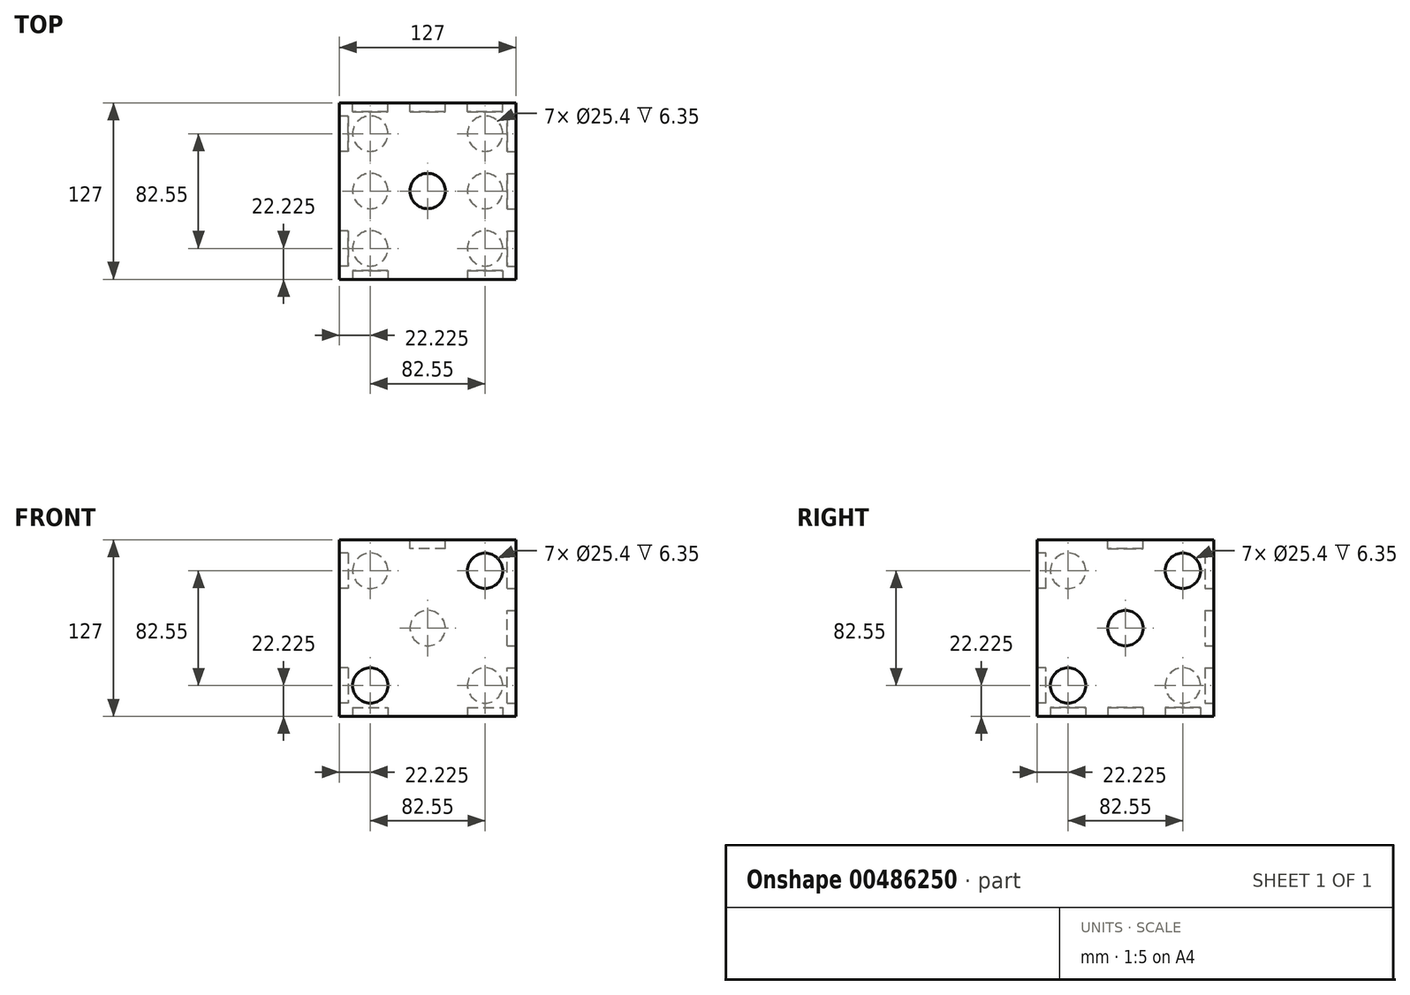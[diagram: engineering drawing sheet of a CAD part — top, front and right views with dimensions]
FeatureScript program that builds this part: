
annotation { "Feature Type Name" : "Feature", "Feature Type Description" : "" }
export const myFeature = defineFeature(function(context is Context, id is Id, definition is map)
    precondition{}
    {
        {
            var Q0;
            Q0=qCreatedBy(makeId("Top.planeOp"),FACE);
            var sketch = newSketch(context, id + "F0", { "sketchPlane" : qUnion([Q0])});
            skLineSegment(sketch, "E0.bottom", {"start": v(0, 0) * mm, "end": v(127, 0) * mm});
            skLineSegment(sketch, "E0.top", {"start": v(0, 127) * mm, "end": v(127, 127) * mm});
            skLineSegment(sketch, "E0.left", {"start": v(0, 0) * mm, "end": v(0, 127) * mm});
            skLineSegment(sketch, "E0.right", {"start": v(127, 0) * mm, "end": v(127, 127) * mm});
            skSolve(sketch);
        }
        {
            var Q0;
            Q0 = qSketchRegion(id + "F0", true);
            extrude(context, id + "F1", {"entities" : qUnion([Q0]), "depth" : 127 * mm});
        }
        {
            var Q0;
            Q0=makeQuery(id+"F1.opExtrude","CAP_FACE",FACE,{"disambiguationData":[OSD([sQuery(id+"F0.wireOp",EDGE,"E0.bottom"),sQuery(id+"F0.wireOp",EDGE,"E0.top"),sQuery(id+"F0.wireOp",EDGE,"E0.left"),sQuery(id+"F0.wireOp",EDGE,"E0.right")])],"isStart":false});
            var sketch = newSketch(context, id + "F2", { "sketchPlane" : qUnion([Q0])});
            skCircle(sketch, "E1", {"center": v(63.5, 63.5) * mm, "radius": 12.7 * mm});
            skPoint(sketch, "E1.centerSnap0", {"position": v(0, 63.5) * mm});
            skPoint(sketch, "E1.centerSnap1", {"position": v(63.5, 127) * mm});
            skSolve(sketch);
        }
        {
            var Q0;
            Q0 = qSketchRegion(id + "F2", true);
            extrude(context, id + "F3", {"entities" : qUnion([Q0]), "operationType" : NewBodyOperationType.REMOVE, "oppositeDirection" : true, "depth" : 6.35 * mm});
        }
        {
            var Q0;
            Q0=makeQuery(id+"F1.opExtrude","SWEPT_FACE",FACE,{"disambiguationData":[OSD([sQuery(id+"F0.wireOp",EDGE,"E0.bottom")])]});
            var sketch = newSketch(context, id + "F4", { "sketchPlane" : qUnion([Q0])});
            skCircle(sketch, "E2", {"center": v(22.23, 22.22) * mm, "radius": 12.7 * mm});
            skCircle(sketch, "E3", {"center": v(104.77, 104.78) * mm, "radius": 12.7 * mm});
            skSolve(sketch);
        }
        {
            var Q0;
            Q0 = qSketchRegion(id + "F4", true);
            extrude(context, id + "F5", {"entities" : qUnion([Q0]), "operationType" : NewBodyOperationType.REMOVE, "oppositeDirection" : true, "depth" : 6.35 * mm});
        }
        {
            var Q0;
            Q0=makeQuery(id+"F1.opExtrude","SWEPT_FACE",FACE,{"disambiguationData":[OSD([sQuery(id+"F0.wireOp",EDGE,"E0.right")])]});
            var sketch = newSketch(context, id + "F6", { "sketchPlane" : qUnion([Q0])});
            skCircle(sketch, "E4", {"center": v(22.23, 22.22) * mm, "radius": 12.7 * mm});
            skCircle(sketch, "E5", {"center": v(63.5, 63.5) * mm, "radius": 12.7 * mm});
            skPoint(sketch, "E5.centerSnap0", {"position": v(63.5, 127) * mm});
            skPoint(sketch, "E5.centerSnap1", {"position": v(0, 63.5) * mm});
            skCircle(sketch, "E6", {"center": v(104.77, 104.78) * mm, "radius": 12.7 * mm});
            skSolve(sketch);
        }
        {
            var Q0;
            Q0 = qSketchRegion(id + "F6", true);
            extrude(context, id + "F7", {"entities" : qUnion([Q0]), "operationType" : NewBodyOperationType.REMOVE, "oppositeDirection" : true, "depth" : 6.35 * mm});
        }
        {
            var Q0;
            Q0=makeQuery(id+"F1.opExtrude","SWEPT_FACE",FACE,{"disambiguationData":[OSD([sQuery(id+"F0.wireOp",EDGE,"E0.top")])]});
            var sketch = newSketch(context, id + "F8", { "sketchPlane" : qUnion([Q0])});
            skLineSegment(sketch, "E7", {"start": v(-127, 127) * mm, "end": v(0, 0) * mm, "construction": true});
            skLineSegment(sketch, "E8", {"start": v(0, 127) * mm, "end": v(-127, 0) * mm, "construction": true});
            skCircle(sketch, "E9", {"center": v(-63.5, 63.5) * mm, "radius": 12.7 * mm});
            skCircle(sketch, "E10", {"center": v(-22.23, 104.78) * mm, "radius": 12.7 * mm});
            skCircle(sketch, "E11", {"center": v(-104.78, 104.78) * mm, "radius": 12.7 * mm});
            skCircle(sketch, "E12", {"center": v(-104.78, 22.23) * mm, "radius": 12.7 * mm});
            skCircle(sketch, "E13", {"center": v(-22.23, 22.23) * mm, "radius": 12.7 * mm});
            skSolve(sketch);
        }
        {
            var Q0;
            Q0 = qSketchRegion(id + "F8", true);
            extrude(context, id + "F9", {"entities" : qUnion([Q0]), "operationType" : NewBodyOperationType.REMOVE, "oppositeDirection" : true, "depth" : 6.35 * mm, "offsetDistance" : 25.4 * mm});
        }
        {
            var Q0;
            Q0=makeQuery(id+"F1.opExtrude","SWEPT_FACE",FACE,{"disambiguationData":[OSD([sQuery(id+"F0.wireOp",EDGE,"E0.left")])]});
            var sketch = newSketch(context, id + "F10", { "sketchPlane" : qUnion([Q0])});
            skLineSegment(sketch, "E14", {"start": v(-127, 127) * mm, "end": v(0, 0) * mm, "construction": true});
            skLineSegment(sketch, "E15", {"start": v(0, 127) * mm, "end": v(-127, 0) * mm, "construction": true});
            skCircle(sketch, "E16", {"center": v(-104.77, 104.77) * mm, "radius": 12.7 * mm});
            skCircle(sketch, "E17", {"center": v(-22.22, 104.77) * mm, "radius": 12.7 * mm});
            skCircle(sketch, "E18", {"center": v(-22.22, 22.23) * mm, "radius": 12.7 * mm});
            skCircle(sketch, "E19", {"center": v(-104.77, 22.23) * mm, "radius": 12.7 * mm});
            skSolve(sketch);
        }
        {
            var Q0;
            Q0 = qSketchRegion(id + "F10", true);
            extrude(context, id + "F11", {"entities" : qUnion([Q0]), "operationType" : NewBodyOperationType.REMOVE, "oppositeDirection" : true, "depth" : 6.35 * mm, "offsetDistance" : 25.4 * mm});
        }
        {
            var Q0;
            Q0=makeQuery(id+"F1.opExtrude","CAP_FACE",FACE,{"disambiguationData":[OSD([sQuery(id+"F0.wireOp",EDGE,"E0.bottom"),sQuery(id+"F0.wireOp",EDGE,"E0.top"),sQuery(id+"F0.wireOp",EDGE,"E0.left"),sQuery(id+"F0.wireOp",EDGE,"E0.right")])],"isStart":true});
            var sketch = newSketch(context, id + "F12", { "sketchPlane" : qUnion([Q0])});
            skLineSegment(sketch, "E20", {"start": v(104.78, -127) * mm, "end": v(104.77, 0) * mm, "construction": true});
            skLineSegment(sketch, "E21", {"start": v(22.23, -127) * mm, "end": v(22.22, 0) * mm, "construction": true});
            skLineSegment(sketch, "E22", {"start": v(127, -104.77) * mm, "end": v(0, -104.77) * mm, "construction": true});
            skLineSegment(sketch, "E23", {"start": v(127, -22.22) * mm, "end": v(0, -22.23) * mm, "construction": true});
            skLineSegment(sketch, "E24", {"start": v(63.5, 0) * mm, "end": v(63.5, -127) * mm, "construction": true});
            skLineSegment(sketch, "E25", {"start": v(127, -63.5) * mm, "end": v(0, -63.5) * mm, "construction": true});
            skCircle(sketch, "E26", {"center": v(104.78, -22.22) * mm, "radius": 12.7 * mm});
            skCircle(sketch, "E27", {"center": v(104.78, -63.5) * mm, "radius": 12.7 * mm});
            skCircle(sketch, "E28", {"center": v(104.78, -104.77) * mm, "radius": 12.7 * mm});
            skCircle(sketch, "E29", {"center": v(22.23, -104.77) * mm, "radius": 12.7 * mm});
            skCircle(sketch, "E30", {"center": v(22.22, -63.5) * mm, "radius": 12.7 * mm});
            skCircle(sketch, "E31", {"center": v(22.22, -22.23) * mm, "radius": 12.7 * mm});
            skSolve(sketch);
        }
        {
            var Q0;
            Q0 = qSketchRegion(id + "F12", true);
            extrude(context, id + "F13", {"entities" : qUnion([Q0]), "operationType" : NewBodyOperationType.REMOVE, "oppositeDirection" : true, "depth" : 6.35 * mm, "offsetDistance" : 25.4 * mm});
        }
    });
